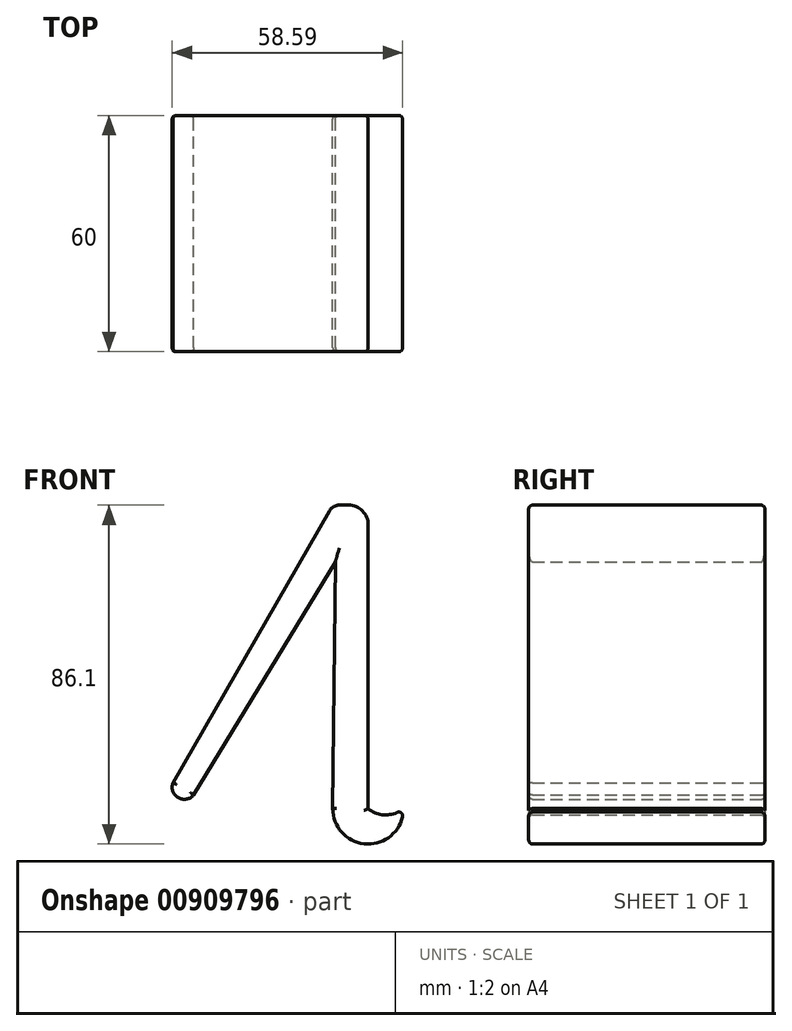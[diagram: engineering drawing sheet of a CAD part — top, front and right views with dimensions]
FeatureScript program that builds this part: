
annotation { "Feature Type Name" : "Feature", "Feature Type Description" : "" }
export const myFeature = defineFeature(function(context is Context, id is Id, definition is map)
    precondition{}
    {
        {
            var Q0;
            Q0=qCreatedBy(makeId("Front.planeOp"),FACE);
            var sketch = newSketch(context, id + "F0", { "sketchPlane" : qUnion([Q0])});
            skLineSegment(sketch, "E0", {"start": v(0, 0) * mm, "end": v(0, 33.5) * mm});
            skLineSegment(sketch, "E1", {"start": v(0, 0) * mm, "end": v(0, -38.5) * mm});
            skLineSegment(sketch, "E2", {"start": v(-5, 38.5) * mm, "end": v(-7.27, 38.5) * mm});
            skArc(sketch, "E3", {"start": v(-9, -38.6) * mm, "mid": v(0.05, -47.6) * mm, "end": v(9, -38.5) * mm});
            skArc(sketch, "E4", {"start": v(0, -38.6) * mm, "mid": v(4.52, -40.21) * mm, "end": v(9, -38.5) * mm});
            skLineSegment(sketch, "E5", {"start": v(-9.87, 37) * mm, "end": v(-45.99, -25.75) * mm});
            skPoint(sketch, "E6.visualSharp", {"position": v(-53.39, -38.6) * mm});
            skPoint(sketch, "E7.visualSharp", {"position": v(-44.7, -36.23) * mm});
            skPoint(sketch, "E8.newPointA", {"position": v(-9, 38.5) * mm});
            skPoint(sketch, "E9.visualSharp", {"position": v(0, 38.5) * mm});
            skArc(sketch, "E9.filletArc", {"start": v(0, 33.5) * mm, "mid": v(-1.46, 37.04) * mm, "end": v(-5, 38.5) * mm});
            skArc(sketch, "E10.filletArc", {"start": v(-7.27, 38.5) * mm, "mid": v(-8.77, 38.1) * mm, "end": v(-9.87, 37) * mm});
            skLineSegment(sketch, "E11", {"start": v(0, 33.5) * mm, "end": v(0, -38.6) * mm});
            skArc(sketch, "E12", {"start": v(-39.57, -27.3) * mm, "mid": v(-39.53, -27.24) * mm, "end": v(-39.49, -27.17) * mm});
            skLineSegment(sketch, "E13", {"start": v(-39.49, -27.17) * mm, "end": v(-8.35, 24.03) * mm});
            skLineSegment(sketch, "E14", {"start": v(-8.35, 24.03) * mm, "end": v(-9, -38.6) * mm});
            skLineSegment(sketch, "E15", {"start": v(-39.49, -27.17) * mm, "end": v(-68.29, -74.54) * mm});
            skLineSegment(sketch, "E16", {"start": v(-45.99, -25.75) * mm, "end": v(-74.35, -75.02) * mm});
            skArc(sketch, "E17", {"start": v(-49.6, -32.01) * mm, "mid": v(-47.87, -36.02) * mm, "end": v(-43.85, -34.34) * mm});
            skSolve(sketch);
        }
        {
            var Q0;
            Q0=makeQuery(id+"F0.imprint","IMPRINT",FACE,{"disambiguationData":[TD([[makeQuery(id+"F0.imprint","IMPRINT",EDGE,{"derivedFrom":sQuery(id+"F0.wireOp",EDGE,"E2")}),1.0]])]});
            extrude(context, id + "F1", {"entities" : qUnion([Q0]), "depth" : 60 * mm, "offsetDistance" : 25 * mm});
        }
        {
            var Q0;
            Q0=makeQuery(id+"F1.opExtrude","SWEPT_EDGE",EDGE,{"disambiguationData":[OSD([sQuery(id+"F0.wireOp",EDGE,"E3"),sQuery(id+"F0.wireOp",EDGE,"E4")])]});
            fillet(context, id + "F2", {"entities" : qUnion([Q0]), "radius" : 1 * mm, "tangentPropagation" : true, "allowEdgeOverflow" : false});
        }
        {
            var Q0;
            Q0=makeQuery(id+"F1.opExtrude","CAP_EDGE",EDGE,{"disambiguationData":[OSD([sQuery(id+"F0.wireOp",EDGE,"E13"),sQuery(id+"F0.wireOp",EDGE,"E15")])],"isStart":false});
            var Q1;
            Q1=makeQuery(id+"F1.opExtrude","CAP_EDGE",EDGE,{"disambiguationData":[OSD([sQuery(id+"F0.wireOp",EDGE,"E5"),sQuery(id+"F0.wireOp",EDGE,"E16")])],"isStart":false});
            var Q2;
            Q2=makeQuery(id+"F1.opExtrude","CAP_EDGE",EDGE,{"disambiguationData":[OSD([sQuery(id+"F0.wireOp",EDGE,"E14")])],"isStart":false});
            var Q3;
            Q3=makeQuery(id+"F1.opExtrude","CAP_EDGE",EDGE,{"disambiguationData":[OSD([sQuery(id+"F0.wireOp",EDGE,"E3")])],"isStart":false});
            var Q4;
            Q4=makeQuery(id+"F1.opExtrude","CAP_EDGE",EDGE,{"disambiguationData":[OSD([sQuery(id+"F0.wireOp",EDGE,"E17")])],"isStart":false});
            fillet(context, id + "F3", {"entities" : qUnion([Q0, Q1, Q2, Q3, Q4]), "radius" : 1 * mm, "tangentPropagation" : true, "allowEdgeOverflow" : false});
        }
        {
            var Q0;
            Q0=makeQuery(id+"F1.opExtrude","CAP_EDGE",EDGE,{"disambiguationData":[OSD([sQuery(id+"F0.wireOp",EDGE,"E5"),sQuery(id+"F0.wireOp",EDGE,"E16")])],"isStart":true});
            var Q1;
            Q1=makeQuery(id+"F1.opExtrude","CAP_EDGE",EDGE,{"disambiguationData":[OSD([sQuery(id+"F0.wireOp",EDGE,"E13"),sQuery(id+"F0.wireOp",EDGE,"E15")])],"isStart":true});
            var Q2;
            Q2=makeQuery(id+"F1.opExtrude","CAP_EDGE",EDGE,{"disambiguationData":[OSD([sQuery(id+"F0.wireOp",EDGE,"E14")])],"isStart":true});
            var Q3;
            Q3=makeQuery(id+"F1.opExtrude","CAP_EDGE",EDGE,{"disambiguationData":[OSD([sQuery(id+"F0.wireOp",EDGE,"E11")])],"isStart":true});
            var Q4;
            Q4=makeQuery(id+"F1.opExtrude","CAP_EDGE",EDGE,{"disambiguationData":[OSD([sQuery(id+"F0.wireOp",EDGE,"E9.filletArc")])],"isStart":true});
            var Q5;
            Q5=makeQuery(id+"F1.opExtrude","CAP_EDGE",EDGE,{"disambiguationData":[OSD([sQuery(id+"F0.wireOp",EDGE,"E10.filletArc")])],"isStart":true});
            var Q6;
            Q6=makeQuery(id+"F1.opExtrude","CAP_EDGE",EDGE,{"disambiguationData":[OSD([sQuery(id+"F0.wireOp",EDGE,"E2")])],"isStart":true});
            var Q7;
            Q7=makeQuery(id+"F1.opExtrude","CAP_EDGE",EDGE,{"disambiguationData":[OSD([sQuery(id+"F0.wireOp",EDGE,"E3")])],"isStart":true});
            var Q8;
            Q8=makeQuery(id+"F1.opExtrude","CAP_EDGE",EDGE,{"disambiguationData":[OSD([sQuery(id+"F0.wireOp",EDGE,"E4")])],"isStart":true});
            var Q9;
            {var subQ0=sQuery(id+"F0.wireOp",EDGE,"E4");var subQ1=sQuery(id+"F0.wireOp",EDGE,"E3");Q9=makeQuery(id+"F2.opFillet","BLEND_EDGE",EDGE,{"blendedFrom":[makeQuery(id+"F1.opExtrude","SWEPT_EDGE",EDGE,{"disambiguationData":[OSD([subQ1,subQ0])]}),makeQuery(id+"F1.opExtrude","CAP_FACE",FACE,{"disambiguationData":[OSD([sQuery(id+"F0.wireOp",EDGE,"E2"),subQ1,subQ0,sQuery(id+"F0.wireOp",EDGE,"E5"),sQuery(id+"F0.wireOp",EDGE,"E9.filletArc"),sQuery(id+"F0.wireOp",EDGE,"E10.filletArc"),sQuery(id+"F0.wireOp",EDGE,"E11"),sQuery(id+"F0.wireOp",EDGE,"E13"),sQuery(id+"F0.wireOp",EDGE,"E14"),sQuery(id+"F0.wireOp",EDGE,"E15"),sQuery(id+"F0.wireOp",EDGE,"E16"),sQuery(id+"F0.wireOp",EDGE,"E17")])],"isStart":true})],"blendedInto":[makeQuery(id+"F1.opExtrude","CAP_FACE",FACE,{"disambiguationData":[OSD([sQuery(id+"F0.wireOp",EDGE,"E2"),subQ1,subQ0,sQuery(id+"F0.wireOp",EDGE,"E5"),sQuery(id+"F0.wireOp",EDGE,"E9.filletArc"),sQuery(id+"F0.wireOp",EDGE,"E10.filletArc"),sQuery(id+"F0.wireOp",EDGE,"E11"),sQuery(id+"F0.wireOp",EDGE,"E13"),sQuery(id+"F0.wireOp",EDGE,"E14"),sQuery(id+"F0.wireOp",EDGE,"E15"),sQuery(id+"F0.wireOp",EDGE,"E16"),sQuery(id+"F0.wireOp",EDGE,"E17")])],"isStart":true})]});}
            var Q10;
            Q10=makeQuery(id+"F1.opExtrude","CAP_EDGE",EDGE,{"disambiguationData":[OSD([sQuery(id+"F0.wireOp",EDGE,"E17")])],"isStart":true});
            fillet(context, id + "F4", {"entities" : qUnion([Q0, Q1, Q2, Q3, Q4, Q5, Q6, Q7, Q8, Q9, Q10]), "radius" : 1 * mm, "tangentPropagation" : true, "allowEdgeOverflow" : false});
        }
    });
